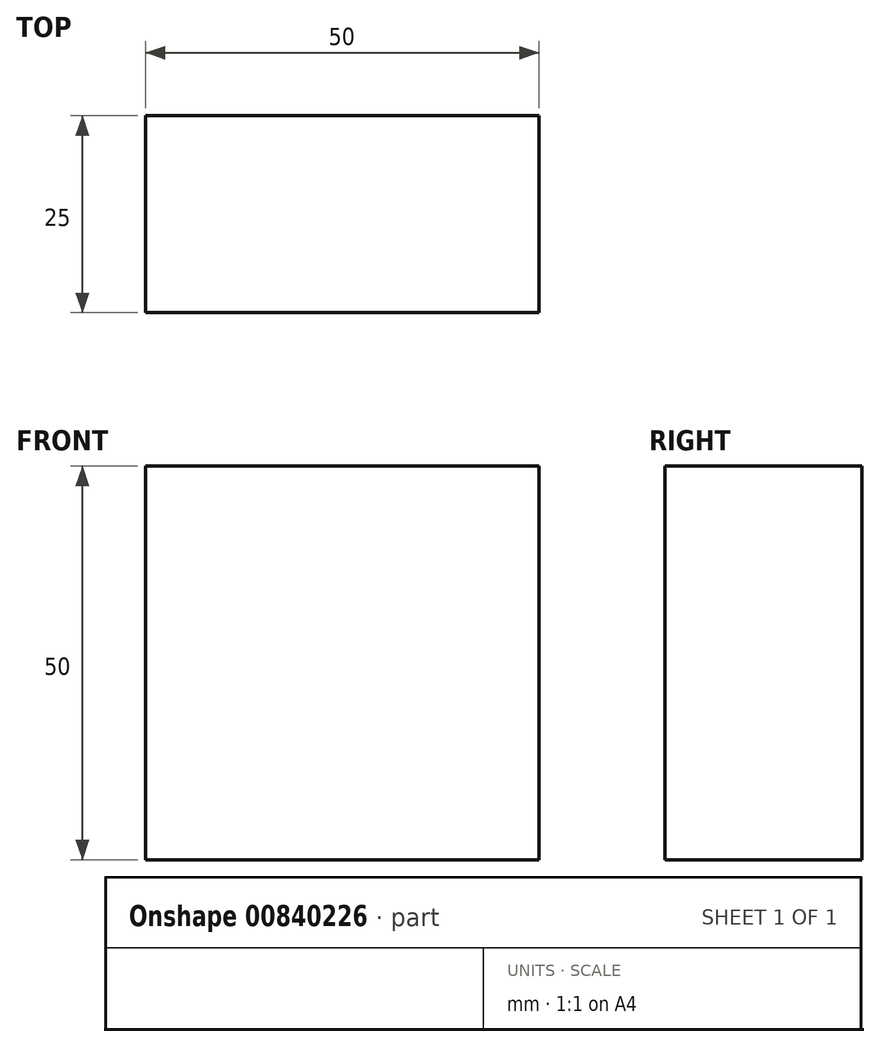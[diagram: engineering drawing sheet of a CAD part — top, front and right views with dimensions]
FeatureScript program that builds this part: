
annotation { "Feature Type Name" : "Feature", "Feature Type Description" : "" }
export const myFeature = defineFeature(function(context is Context, id is Id, definition is map)
    precondition{}
    {
        {
            var Q0;
            Q0=qCreatedBy(makeId("Front.planeOp"),FACE);
            var sketch = newSketch(context, id + "F0", { "sketchPlane" : qUnion([Q0])});
            skLineSegment(sketch, "E0.bottom", {"start": v(25, -25) * mm, "end": v(-25, -25) * mm});
            skLineSegment(sketch, "E0.top", {"start": v(25, 25) * mm, "end": v(-25, 25) * mm});
            skLineSegment(sketch, "E0.left", {"start": v(25, -25) * mm, "end": v(25, 25) * mm});
            skLineSegment(sketch, "E0.right", {"start": v(-25, -25) * mm, "end": v(-25, 25) * mm});
            skPoint(sketch, "E0.middle", {"position": v(0, 0) * mm});
            skSolve(sketch);
        }
        {
            var Q0;
            Q0 = qSketchRegion(id + "F0", true);
            extrude(context, id + "F1", {"entities" : qUnion([Q0]), "endBound" : BoundingType.SYMMETRIC, "depth" : 25 * mm, "offsetDistance" : 25 * mm});
        }
    });
